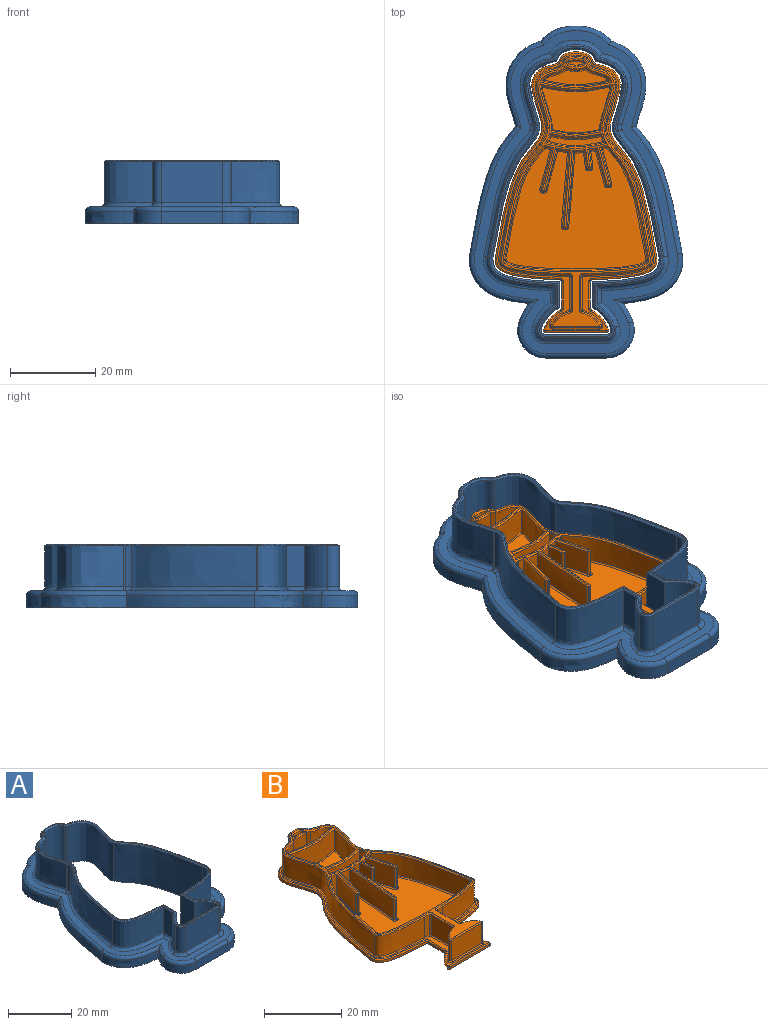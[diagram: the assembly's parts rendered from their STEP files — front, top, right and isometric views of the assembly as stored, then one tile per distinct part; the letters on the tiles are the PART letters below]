
ASSEMBLY  parts=2 mates=1
PART A: 111 faces, bbox 51.5x85.8x16.5 mm
  f0: extruded ~29.42x10.79mm, area 308.9mm2, adj f1,f13,f51,f75
  f1: extruded ~15.68x9.7mm, area 186.8mm2, adj f0,f29,f49,f73
  f2: cylinder r=9.66mm len=9.7mm, axis (0,0,-1), area 67.2mm2, adj f3,f29,f52,f69
  f3: cylinder r=2.09mm len=9.7mm, axis (0,0,-1), area 38.3mm2, adj f2,f4,f54,f67
  f4: plane 14.39x9.7mm, normal (0,-1,0), area 139.6mm2, adj f3,f5,f56,f68
  f5: cylinder r=2.09mm len=9.7mm, axis (0,0,-1), area 38.3mm2, adj f4,f6,f58,f70
  f6: cylinder r=9.66mm len=9.7mm, axis (0,0,-1), area 67.2mm2, adj f5,f30,f60,f72
  f7: extruded ~15.65x9.7mm, area 184.8mm2, adj f8,f30,f64,f76
  f8: plane 9.7x0.14mm, normal (-0.99,0.15,0), area 1.4mm2, adj f7,f31,f64,f66,f78
  f9: extruded ~9.7x0.34mm, area 3.3mm2, adj f10,f32,f61,f84
  f10: extruded ~15.59x9.7mm, area 189.2mm2, adj f9,f11,f59,f83
  f11: extruded ~10.77x9.7mm, area 126.7mm2, adj f10,f12,f57,f81
  f12: extruded ~15.59x9.7mm, area 189.2mm2, adj f11,f13,f55,f79
  f13: extruded ~9.7x1.79mm, area 17.6mm2, adj f0,f12,f53,f77
  f14: plane 14.65x6.04mm, normal (-1,0,0), area 88.5mm2, adj f15,f33,f35,f108
  f15: extruded ~15.68x14.65mm, area 270.2mm2, adj f14,f16,f35,f106
  f16: extruded ~29.26x14.65mm, area 464.1mm2, adj f15,f17,f35,f104
  f17: extruded ~16.71x14.65mm, area 298.4mm2, adj f16,f18,f35,f102
  f18: extruded ~14.71x0.53mm, area 10.7mm2, adj f17,f19,f35,f97,f102
  f19: extruded ~14.65x8.84mm, area 158.4mm2, adj f18,f20,f35,f97
  f20: extruded ~14.71x0.53mm, area 10.7mm2, adj f19,f21,f35,f97,f98
  f21: extruded ~16.71x14.65mm, area 298.4mm2, adj f20,f22,f35,f98
  f22: extruded ~29.33x14.65mm, area 465.2mm2, adj f21,f23,f35,f99
  f23: extruded ~15.66x14.65mm, area 268.6mm2, adj f22,f24,f35,f100
  f24: plane 14.65x6.04mm, normal (1,0,0), area 88.5mm2, adj f23,f25,f35,f101
  f25: cylinder r=8.56mm len=14.65mm, axis (0,0,-1), area 98.8mm2, adj f24,f26,f35,f103
  f26: cylinder r=0.99mm len=14.65mm, axis (0,0,-1), area 27.4mm2, adj f25,f27,f35,f105
  f27: plane 14.65x14.39mm, normal (0,1,0), area 210.8mm2, adj f26,f28,f35,f107
  f28: cylinder r=0.99mm len=14.65mm, axis (0,0,-1), area 27.4mm2, adj f27,f33,f35,f109
  f29: plane 9.7x4.33mm, normal (1,0,0), area 42mm2, adj f1,f2,f50,f71
  f30: plane 9.7x4.33mm, normal (-1,0,0), area 42mm2, adj f6,f7,f62,f74
  f31: extruded ~29.44x10.8mm, area 309.1mm2, adj f8,f32,f65,f80
  f32: extruded ~9.7x1.46mm, area 14.3mm2, adj f9,f31,f63,f82
  f33: cylinder r=8.56mm len=14.65mm, axis (0,0,-1), area 98.8mm2, adj f14,f28,f35,f110
  f34: plane 68.72x41.18mm, normal (0,0,1), area 81.6mm2, adj f49,f50,f51,f52,f53,f54,f55,f56
  f35: plane 77.87x50.07mm, normal (0,0,-1), area 1158.8mm2, adj f14,f15,f16,f17,f18,f19,f20,f21
  f36: extruded ~19.98x8.16mm, area 72.4mm2, adj f35,f37,f47,f95
  f37: extruded ~16.48x3.54mm, area 55.8mm2, adj f35,f36,f38,f93
  f38: extruded ~19.98x8.16mm, area 72.4mm2, adj f35,f37,f39,f91
  f39: extruded ~29.84x10.78mm, area 96.8mm2, adj f35,f38,f40,f89
  f40: extruded ~13.94x11.74mm, area 62.3mm2, adj f35,f39,f41,f87
  f41: cylinder r=14.06mm len=4.26mm, axis (0,0,-1), area 14.5mm2, adj f35,f40,f42,f85
  f42: cylinder r=6.49mm len=8.51mm, axis (0,0,-1), area 36.7mm2, adj f35,f41,f43,f86
  f43: plane 14.39x3mm, normal (0,-1,0), area 43.2mm2, adj f35,f42,f44,f88
  f44: cylinder r=6.49mm len=8.51mm, axis (0,0,-1), area 36.7mm2, adj f35,f43,f45,f90
  f45: cylinder r=14.06mm len=4.26mm, axis (0,0,-1), area 14.6mm2, adj f35,f44,f46,f92
  f46: extruded ~13.93x11.59mm, area 61.7mm2, adj f35,f45,f47,f94
  f47: extruded ~29.99x10.81mm, area 97.2mm2, adj f35,f36,f46,f96
  f48: plane 77.12x49.55mm, normal (0,0,1), area 462.9mm2, adj f67,f68,f69,f70,f71,f72,f73,f74
  f49: bspline ~17x7.57mm, area 8.6mm2, adj f1,f34,f50,f51
  f50: plane 4.83x0.33mm, normal (0.67,0,0.74), area 2mm2, adj f29,f34,f49,f52
  f51: bspline ~31.04x11.35mm, area 14.2mm2, adj f0,f34,f49,f53
  f52: cone r=9.66mm half-angle=47.7deg, axis (0,0,-1), area 3.1mm2, adj f2,f34,f50,f54
  f53: bspline ~1.96x0.54mm, area 0.8mm2, adj f13,f34,f51,f55
  f54: cone r=2.09mm half-angle=47.7deg, axis (0,0,-1), area 1.6mm2, adj f3,f34,f52,f56
  f55: bspline ~15.91x7.86mm, area 8.6mm2, adj f12,f34,f53,f57
  f56: plane 14.39x0.33mm, normal (0,-0.67,0.74), area 6.4mm2, adj f4,f34,f54,f58
  f57: bspline ~10.89x3.19mm, area 5.7mm2, adj f11,f34,f55,f59
  f58: cone r=2.09mm half-angle=47.7deg, axis (0,0,-1), area 1.6mm2, adj f5,f34,f56,f60
  f59: bspline ~15.91x7.86mm, area 8.6mm2, adj f10,f34,f57,f61
  f60: cone r=9.66mm half-angle=47.7deg, axis (0,0,-1), area 3.1mm2, adj f6,f34,f58,f62
  f61: bspline ~0.4x0.38mm, area 0.2mm2, adj f9,f34,f59,f63
  f62: plane 4.84x0.33mm, normal (-0.67,0,0.74), area 2mm2, adj f30,f34,f60,f64
  f63: bspline ~1.61x0.5mm, area 0.7mm2, adj f32,f34,f61,f65
  f64: bspline ~17.44x7.46mm, area 8.5mm2, adj f7,f8,f34,f62,f66
  f65: bspline ~32.87x11.64mm, area 14.2mm2, adj f31,f34,f63,f66
  f66: plane 0.34x0.3mm, normal (-0.66,0.1,0.74), area 0mm2, adj f8,f34,f64,f65
  f67: bspline ~17.16x8.58mm, area 7.8mm2, adj f3,f48,f68,f69
  f68: extruded ~14.39x1.1mm, area 23.7mm2, adj f4,f48,f67,f70
  f69: bspline ~23.72x23.72mm, area 11.3mm2, adj f2,f48,f67,f71
  f70: bspline ~4.18x3.19mm, area 7.8mm2, adj f5,f48,f68,f72
  f71: extruded ~4.33x1.1mm, area 5.9mm2, adj f29,f48,f69,f73
  f72: bspline ~23.72x23.72mm, area 11.3mm2, adj f6,f48,f70,f74
  f73: bspline ~16.94x8.46mm, area 32.1mm2, adj f1,f48,f71,f75
  f74: extruded ~4.33x1.1mm, area 5.9mm2, adj f30,f48,f72,f76
  f75: bspline ~29.96x11.92mm, area 52.6mm2, adj f0,f48,f73,f77
  f76: bspline ~16.92x8.24mm, area 31.7mm2, adj f7,f48,f74,f78
  f77: bspline ~1.79x1.19mm, area 2.6mm2, adj f13,f48,f75,f79
  f78: extruded ~1.11x1mm, area 0.2mm2, adj f8,f48,f76,f80
  f79: bspline ~16.88x7.89mm, area 32.8mm2, adj f12,f48,f77,f81
  f80: bspline ~29.99x11.93mm, area 52.7mm2, adj f31,f48,f78,f82
  f81: bspline ~12.89x4.11mm, area 22.3mm2, adj f11,f48,f79,f83
  f82: bspline ~1.46x1.18mm, area 2.1mm2, adj f32,f48,f80,f84
  f83: bspline ~16.88x7.89mm, area 32.8mm2, adj f10,f48,f81,f84
  f84: bspline ~1.14x1mm, area 0.5mm2, adj f9,f48,f82,f83
  f85: bspline ~28.12x28.12mm, area 9.8mm2, adj f41,f48,f86,f87
  f86: bspline ~25.96x12.98mm, area 18.9mm2, adj f42,f48,f85,f88
  f87: bspline ~16.36x12.12mm, area 35mm2, adj f40,f48,f85,f89
  f88: extruded ~14.39x1.1mm, area 23.7mm2, adj f43,f48,f86,f90
  f89: bspline ~30.77x12.11mm, area 53.3mm2, adj f39,f48,f87,f91
  f90: bspline ~8.51x6.49mm, area 18.9mm2, adj f44,f48,f88,f92
  f91: bspline ~20.56x8.81mm, area 39.5mm2, adj f38,f48,f89,f93
  f92: bspline ~28.12x28.12mm, area 9.8mm2, adj f45,f48,f90,f94
  f93: bspline ~17.04x4.59mm, area 30mm2, adj f37,f48,f91,f95
  f94: bspline ~16.34x11.96mm, area 34.7mm2, adj f46,f48,f92,f96
  f95: bspline ~20.56x8.81mm, area 39.5mm2, adj f36,f48,f93,f96
  f96: bspline ~30.72x12.1mm, area 53.6mm2, adj f47,f48,f94,f95
  f97: bspline ~9.95x3.4mm, area 6.1mm2, adj f18,f19,f20,f34,f98,f102
  f98: bspline ~17.35x7.19mm, area 10.9mm2, adj f20,f21,f34,f97,f99
  f99: bspline ~29.45x11.15mm, area 16.5mm2, adj f22,f34,f98,f100
  f100: bspline ~17.11x6.15mm, area 9.6mm2, adj f23,f34,f99,f101
  f101: plane 6.04x0.39mm, normal (0.67,0,0.74), area 3mm2, adj f24,f34,f100,f103
  f102: bspline ~17.35x7.19mm, area 10.9mm2, adj f17,f18,f34,f97,f104
  f103: cone r=8.94mm half-angle=47.7deg, axis (0,0,1), area 3.5mm2, adj f25,f34,f101,f105
  f104: bspline ~30.95x11.38mm, area 16.5mm2, adj f16,f34,f102,f106
  f105: cone r=1.38mm half-angle=47.7deg, axis (0,0,1), area 1.2mm2, adj f26,f34,f103,f107
  f106: bspline ~17.04x6.75mm, area 9.7mm2, adj f15,f34,f104,f108
  f107: plane 14.39x0.39mm, normal (0,0.67,0.74), area 7.5mm2, adj f27,f34,f105,f109
  f108: plane 6.04x0.39mm, normal (-0.67,0,0.74), area 3mm2, adj f14,f34,f106,f110
  f109: cone r=1.38mm half-angle=47.7deg, axis (0,0,1), area 1.2mm2, adj f28,f34,f107,f110
  f110: cone r=8.94mm half-angle=47.7deg, axis (0,0,1), area 3.5mm2, adj f33,f34,f108,f109
PART B: 264 faces, bbox 38.5x68.2x8.5 mm
  f0: plane 6.21x0.7mm, normal (1,0,0), area 4.3mm2, adj f1,f261,f262,f263
  f1: plane 65.77x37.97mm, normal (0,0,-1), area 1480.6mm2, adj f0,f2,f249,f250,f251,f252,f253,f254
  f2: cylinder r=0.44mm len=0.7mm, axis (0,0,-1), area 0.6mm2, adj f1,f3,f249,f260
  f3: bspline ~0.58x0.44mm, area 0.3mm2, adj f2,f4,f16,f248
  f4: extruded ~14.39x0.33mm, area 7.1mm2, adj f3,f5,f16,f260
  f5: bspline ~1.76x0.88mm, area 0.3mm2, adj f4,f6,f16,f259
  f6: bspline ~16.02x16.02mm, area 3.1mm2, adj f5,f7,f16,f258
  f7: bspline ~2.2x2.2mm, area 0.3mm2, adj f6,f8,f16,f257
  f8: extruded ~6.21x0.33mm, area 3.1mm2, adj f7,f9,f16,f256
  f9: bspline ~2.2x2.2mm, area 0.4mm2, adj f8,f10,f16,f255
  f10: bspline ~15.29x5.04mm, area 8.6mm2, adj f9,f11,f16,f254
  f11: bspline ~47.06x15.53mm, area 26.3mm2, adj f10,f12,f16,f253
  f12: bspline ~7.84x2.2mm, area 4.5mm2, adj f11,f13,f16,f252
  f13: bspline ~47x15.52mm, area 26.2mm2, adj f12,f14,f16,f251
  f14: bspline ~15.27x5.21mm, area 8.6mm2, adj f13,f15,f16,f250
  f15: bspline ~4.4x2.2mm, area 0.4mm2, adj f14,f16,f262,f263
  f16: plane 65.52x37.83mm, normal (0,0,1), area 91.8mm2, adj f3,f4,f5,f6,f7,f8,f9,f10
  f17: bspline ~4.4x2.2mm, area 0.3mm2, adj f16,f248,f261,f262
  f18: extruded ~10.94x0.33mm, area 5.4mm2, adj f16,f19,f227,f247
  f19: plane 10.94x6.4mm, normal (0,-1,0), area 70mm2, adj f18,f20,f225,f226
  f20: plane 10.94x0.33mm, normal (0,-0.67,0.74), area 4.9mm2, adj f19,f21,f60,f224
  f21: cone r=0.44mm half-angle=47.7deg, axis (0,0,-1), area 0.3mm2, adj f20,f22,f60,f226
  f22: cone r=6.91mm half-angle=47.7deg, axis (0,0,-1), area 2.4mm2, adj f21,f23,f59,f60
  f23: cylinder r=6.91mm len=6.4mm, axis (0,0,-1), area 35.2mm2, adj f22,f24,f226,f246
  f24: cylinder r=0.44mm len=6.4mm, axis (0,0,-1), area 3.8mm2, adj f23,f25,f59,f245
  f25: plane 7.66x6.4mm, normal (-1,0,0), area 49mm2, adj f24,f26,f58,f244
  f26: plane 7.66x0.33mm, normal (-0.67,0,0.74), area 3.4mm2, adj f25,f27,f59,f60
  f27: cone r=0.77mm half-angle=47.7deg, axis (0,0,1), area 0.4mm2, adj f26,f28,f58,f60
  f28: bspline ~1.77x0.36mm, area 0.8mm2, adj f27,f29,f57,f60
  f29: extruded ~6.4x1.77mm, area 11.3mm2, adj f28,f30,f58,f242
  f30: extruded ~14.57x6.4mm, area 102.6mm2, adj f29,f31,f57,f241
  f31: extruded ~41.68x10.97mm, area 284.7mm2, adj f30,f32,f56,f240
  f32: extruded ~6.4x5.32mm, area 42.2mm2, adj f31,f33,f55,f239
  f33: extruded ~6.4x1.2mm, area 10mm2, adj f32,f34,f54,f238
  f34: extruded ~6.4x5.72mm, area 43.1mm2, adj f33,f35,f53,f237
  f35: extruded ~6.4x1.2mm, area 10mm2, adj f34,f36,f52,f236
  f36: bspline ~1.5x1.27mm, area 0.8mm2, adj f35,f37,f53,f60
  f37: bspline ~5.49x3.41mm, area 2.9mm2, adj f36,f38,f52,f60
  f38: bspline ~43.88x11.71mm, area 19.8mm2, adj f37,f39,f51,f60
  f39: extruded ~41.64x10.96mm, area 284.5mm2, adj f38,f40,f52,f234
  f40: extruded ~14.59x6.4mm, area 103mm2, adj f39,f41,f51,f233
  f41: extruded ~6.4x1.77mm, area 11.3mm2, adj f40,f42,f50,f232
  f42: cylinder r=0.44mm len=6.4mm, axis (0,0,-1), area 4.4mm2, adj f41,f43,f49,f231
  f43: plane 7.66x6.4mm, normal (1,0,0), area 49mm2, adj f42,f44,f48,f230
  f44: plane 7.66x0.33mm, normal (0.67,0,0.74), area 3.4mm2, adj f43,f45,f49,f60
  f45: cone r=0.77mm half-angle=47.7deg, axis (0,0,1), area 0.4mm2, adj f44,f46,f48,f60
  f46: cone r=6.91mm half-angle=47.7deg, axis (0,0,-1), area 2.4mm2, adj f45,f47,f60,f224
  f47: cylinder r=6.91mm len=6.4mm, axis (0,0,-1), area 35.2mm2, adj f46,f48,f225,f228
  f48: cylinder r=0.44mm len=6.4mm, axis (0,0,-1), area 3.8mm2, adj f43,f45,f47,f229
  f49: cone r=0.77mm half-angle=47.7deg, axis (0,0,1), area 0.4mm2, adj f42,f44,f50,f60
  f50: bspline ~1.77x0.36mm, area 0.8mm2, adj f41,f49,f51,f60
  f51: bspline ~14.6x3.92mm, area 7.1mm2, adj f38,f40,f50,f60
  f52: extruded ~6.4x5.32mm, area 42.2mm2, adj f35,f37,f39,f235
  f53: bspline ~5.85x1.69mm, area 2.8mm2, adj f34,f36,f54,f60
  f54: bspline ~1.51x1.28mm, area 0.7mm2, adj f33,f53,f55,f60
  f55: bspline ~5.49x3.41mm, area 2.9mm2, adj f32,f54,f56,f60
  f56: bspline ~41.73x11.3mm, area 19.8mm2, adj f31,f55,f57,f60
  f57: bspline ~14.64x3.78mm, area 7mm2, adj f28,f30,f56,f60
  f58: cylinder r=0.44mm len=6.4mm, axis (0,0,-1), area 4.4mm2, adj f25,f27,f29,f243
  f59: cone r=0.77mm half-angle=47.7deg, axis (0,0,1), area 0.4mm2, adj f22,f24,f26,f60
  f60: plane 63.39x35.76mm, normal (0,0,1), area 151.5mm2, adj f20,f21,f22,f26,f27,f28,f36,f37
  f61: bspline ~4.24x1.65mm, area 3.9mm2, adj f60,f62
  f62: extruded ~6.7x3.6mm, area 52.3mm2, adj f61,f63
  f63: plane 3.6x1.66mm, normal (0,0,1), area 2.8mm2, adj f62
  f64: bspline ~5.66x1.18mm, area 2.2mm2, adj f60,f65,f78,f82
  f65: extruded ~6.4x4.72mm, area 31.5mm2, adj f64,f66,f76,f77
  f66: extruded ~6.4x0.82mm, area 7.1mm2, adj f65,f67,f75,f78
  f67: bspline ~1.09x1.04mm, area 0.5mm2, adj f66,f68,f74,f76
  f68: bspline ~4.99x2.58mm, area 2.6mm2, adj f67,f69,f74,f75
  f69: bspline ~16.15x1.45mm, area 7.7mm2, adj f68,f70,f73,f74
  f70: bspline ~4.99x2.58mm, area 2.6mm2, adj f69,f71,f72,f74
  f71: bspline ~1.09x1.04mm, area 0.5mm2, adj f70,f74,f76,f77
  f72: extruded ~6.4x4.8mm, area 35.4mm2, adj f70,f73,f77,f81
  f73: extruded ~15.96x6.4mm, area 103.4mm2, adj f69,f72,f75,f80
  f74: plane 15.2x3.78mm, normal (0,0,1), area 32.5mm2, adj f67,f68,f69,f70,f71,f76
  f75: extruded ~6.4x4.8mm, area 35.4mm2, adj f66,f68,f73,f79
  f76: bspline ~5.18x0.91mm, area 2.4mm2, adj f65,f67,f71,f74
  f77: extruded ~6.4x0.82mm, area 7.1mm2, adj f65,f71,f72,f82
  f78: bspline ~1.27x1.24mm, area 0.5mm2, adj f60,f64,f66,f79
  f79: bspline ~5.26x3.07mm, area 2.6mm2, adj f60,f75,f78,f80
  f80: bspline ~18.55x1.73mm, area 7.4mm2, adj f60,f73,f79,f81
  f81: bspline ~5.26x3.07mm, area 2.6mm2, adj f60,f72,f80,f82
  f82: bspline ~1.27x1.24mm, area 0.5mm2, adj f60,f64,f77,f81
  f83: bspline ~18.82x1.73mm, area 7.5mm2, adj f60,f84,f97,f101
  f84: extruded ~16.31x6.5mm, area 107.2mm2, adj f83,f85,f95,f96
  f85: extruded ~10.23x6.5mm, area 68.6mm2, adj f84,f86,f94,f97
  f86: bspline ~10.32x2.63mm, area 3.4mm2, adj f85,f87,f93,f95
  f87: bspline ~0.02x0.02mm, area 0mm2, adj f86,f88,f94
  f88: bspline ~11.25x0.98mm, area 3.7mm2, adj f87,f89,f91,f93
  f89: extruded ~11.25x6.5mm, area 73.9mm2, adj f88,f90,f94,f99
  f90: cylinder r=0.22mm len=6.5mm, axis (0,0,-1), area 2mm2, adj f89,f91,f96,f99,f101
  f91: bspline ~0.44x0.4mm, area 0mm2, adj f88,f90,f92
  f92: bspline ~10.32x2.63mm, area 3.4mm2, adj f91,f93,f95,f96
  f93: plane 16.1x10.99mm, normal (0,0,1), area 126.2mm2, adj f86,f88,f92,f95
  f94: cylinder r=0.22mm len=6.51mm, axis (0,0,-1), area 2mm2, adj f85,f87,f89,f97,f98
  f95: bspline ~16.6x1.36mm, area 5.4mm2, adj f84,f86,f92,f93
  f96: extruded ~10.23x6.5mm, area 68.6mm2, adj f84,f90,f92,f101
  f97: bspline ~12.31x2.79mm, area 4.9mm2, adj f60,f83,f85,f94,f98
  f98: plane 0.56x0.4mm, normal (0.12,0.66,0.74), area 0.1mm2, adj f60,f94,f97,f99
  f99: bspline ~12.38x1.32mm, area 5.2mm2, adj f60,f89,f90,f98,f100,f101
  f100: plane 0.39x0.33mm, normal (-0.13,0.66,0.74), area 0.1mm2, adj f60,f99,f101
  f101: bspline ~12.3x2.79mm, area 4.9mm2, adj f60,f83,f90,f96,f99,f100
  f102: bspline ~2.82x1.46mm, area 1mm2, adj f60,f103,f124,f132
  f103: extruded ~6.4x1.8mm, area 12.5mm2, adj f102,f104,f122,f123
  f104: extruded ~12.01x6.4mm, area 77.7mm2, adj f103,f105,f121,f132
  f105: bspline ~12.3x1.17mm, area 5.9mm2, adj f104,f106,f120,f122
  f106: bspline ~1.95x1.08mm, area 0.8mm2, adj f105,f107,f120,f121
  f107: bspline ~2.3x0.83mm, area 1mm2, adj f106,f108,f119,f120
  f108: bspline ~1.77x0.64mm, area 0.9mm2, adj f107,f109,f118,f120
  f109: bspline ~1.14x0.47mm, area 0.5mm2, adj f108,f110,f117,f120
  f110: bspline ~2.25x0.44mm, area 1.1mm2, adj f109,f111,f116,f120
  f111: bspline ~3.78x0.79mm, area 1.9mm2, adj f110,f112,f115,f120
  f112: bspline ~1.14x0.55mm, area 0.5mm2, adj f111,f113,f114,f120
  f113: bspline ~1.46x0.64mm, area 0.6mm2, adj f112,f120,f122,f123
  f114: extruded ~6.4x1.08mm, area 7mm2, adj f112,f115,f123,f125
  f115: extruded ~6.4x3.77mm, area 24.4mm2, adj f111,f114,f116,f126
  f116: extruded ~6.4x2.25mm, area 14.4mm2, adj f110,f115,f117,f127
  f117: extruded ~6.4x1.1mm, area 7.1mm2, adj f109,f116,f118,f128
  f118: extruded ~6.4x1.72mm, area 11.2mm2, adj f108,f117,f119,f129
  f119: extruded ~6.4x2.22mm, area 14.5mm2, adj f107,f118,f121,f130
  f120: plane 13.06x2.65mm, normal (0,0,1), area 15.9mm2, adj f105,f106,f107,f108,f109,f110,f111,f112
  f121: extruded ~6.4x1.76mm, area 12.3mm2, adj f104,f106,f119,f131
  f122: bspline ~1.99x1.1mm, area 0.8mm2, adj f103,f105,f113,f120
  f123: extruded ~6.4x1.38mm, area 9.1mm2, adj f103,f113,f114,f124
  f124: bspline ~1.98x0.77mm, area 0.7mm2, adj f60,f102,f123,f125
  f125: bspline ~1.15x0.55mm, area 0.5mm2, adj f60,f114,f124,f126
  f126: bspline ~3.84x0.8mm, area 1.7mm2, adj f60,f115,f125,f127
  f127: bspline ~2.3x0.44mm, area 1mm2, adj f60,f116,f126,f128
  f128: bspline ~1.15x0.47mm, area 0.5mm2, adj f60,f117,f127,f129
  f129: bspline ~1.79x0.64mm, area 0.8mm2, adj f60,f118,f128,f130
  f130: bspline ~2.85x0.96mm, area 1.1mm2, adj f60,f119,f129,f131
  f131: bspline ~2.77x1.43mm, area 1mm2, adj f60,f121,f130,f132
  f132: bspline ~13.86x1.36mm, area 5.5mm2, adj f60,f102,f104,f131
  f133: bspline ~17.93x1.79mm, area 8mm2, adj f60,f134,f195,f223
  f134: extruded ~17.59x6.4mm, area 113mm2, adj f133,f135,f193,f194
  f135: extruded ~6.4x2.56mm, area 16.4mm2, adj f134,f136,f192,f223
  f136: bspline ~2.64x0.47mm, area 1.1mm2, adj f135,f137,f191,f193
  f137: plane 33.35x28.72mm, normal (0,0,1), area 671.4mm2, adj f136,f138,f165,f166,f167,f168,f169,f170
  f138: extruded ~0.35x0.3mm, area 0.1mm2, adj f137,f139,f165,f190
  f139: plane 6.4x0.22mm, normal (-0.11,-0.99,0), area 1.4mm2, adj f138,f140,f194,f196
  f140: cylinder r=0.44mm len=6.4mm, axis (0,0,-1), area 4.4mm2, adj f139,f141,f190,f197
  f141: extruded ~17.54x6.4mm, area 112.6mm2, adj f140,f142,f189,f198
  f142: extruded ~6.4x2.87mm, area 18.6mm2, adj f141,f143,f188,f199
  f143: extruded ~9.59x6.4mm, area 63.6mm2, adj f142,f144,f187,f200
  f144: cylinder r=0.44mm len=6.4mm, axis (0,0,-1), area 4.4mm2, adj f143,f145,f186,f201
  f145: plane 6.4x0.21mm, normal (-0.33,-0.94,0), area 1.4mm2, adj f144,f146,f185,f202
  f146: cylinder r=0.44mm len=6.4mm, axis (0,0,-1), area 4.4mm2, adj f145,f147,f184,f203
  f147: extruded ~9.47x6.4mm, area 62.7mm2, adj f146,f148,f183,f204
  f148: extruded ~6.4x1.4mm, area 9.2mm2, adj f147,f149,f182,f205
  f149: plane 6.4x0.38mm, normal (-0.23,-0.97,0), area 2.5mm2, adj f148,f150,f181,f206
  f150: extruded ~26.48x9.36mm, area 182.8mm2, adj f149,f151,f180,f207
  f151: extruded ~33.54x6.4mm, area 223.3mm2, adj f150,f152,f179,f208
  f152: extruded ~26.53x9.4mm, area 183.2mm2, adj f151,f153,f178,f209
  f153: plane 6.4x0.37mm, normal (0.27,-0.96,0), area 2.5mm2, adj f152,f154,f177,f210
  f154: extruded ~6.4x1.16mm, area 7.6mm2, adj f153,f155,f176,f211
  f155: extruded ~8.32x6.4mm, area 55.1mm2, adj f154,f156,f175,f212
  f156: cylinder r=0.44mm len=6.4mm, axis (0,0,-1), area 4.4mm2, adj f155,f157,f174,f213
  f157: plane 6.4x0.21mm, normal (0.24,-0.97,0), area 1.4mm2, adj f156,f158,f173,f214
  f158: cylinder r=0.44mm len=6.4mm, axis (0,0,-1), area 4.4mm2, adj f157,f159,f172,f215
  f159: extruded ~8.36x6.4mm, area 55.4mm2, adj f158,f160,f171,f216
  f160: extruded ~6.4x1.7mm, area 11.1mm2, adj f159,f161,f170,f217
  f161: extruded ~6.4x3.88mm, area 25.1mm2, adj f160,f162,f169,f218
  f162: cylinder r=0.44mm len=6.4mm, axis (0,0,-1), area 4.4mm2, adj f161,f163,f168,f219
  f163: plane 6.4x0.22mm, normal (0.11,-0.99,0), area 1.4mm2, adj f162,f164,f167,f220
  f164: cylinder r=0.44mm len=6.4mm, axis (0,0,-1), area 4.4mm2, adj f163,f166,f192,f221
  f165: bspline ~2.2x2.2mm, area 0.4mm2, adj f137,f138,f193,f194
  f166: bspline ~2.2x2.2mm, area 0.4mm2, adj f137,f164,f167,f191
  f167: extruded ~0.35x0.3mm, area 0.1mm2, adj f137,f163,f166,f168
  f168: bspline ~0.88x0.72mm, area 0.4mm2, adj f137,f162,f167,f169
  f169: bspline ~3.97x0.89mm, area 1.9mm2, adj f137,f161,f168,f170
  f170: bspline ~1.79x0.65mm, area 0.7mm2, adj f137,f160,f169,f171
  f171: bspline ~8.49x2.55mm, area 4.2mm2, adj f137,f159,f170,f172
  f172: bspline ~2.2x2.2mm, area 0.4mm2, adj f137,f158,f171,f173
  f173: extruded ~0.37x0.3mm, area 0.1mm2, adj f137,f157,f172,f174
  f174: bspline ~0.94x0.67mm, area 0.4mm2, adj f137,f156,f173,f175
  f175: bspline ~8.45x2.54mm, area 4.2mm2, adj f137,f155,f174,f176
  f176: bspline ~1.26x0.6mm, area 0.5mm2, adj f137,f154,f175,f177
  f177: extruded ~0.47x0.42mm, area 0.1mm2, adj f137,f153,f176,f178
  f178: bspline ~26.91x9.8mm, area 14.1mm2, adj f137,f152,f177,f179
  f179: bspline ~33.57x2.58mm, area 17.1mm2, adj f137,f151,f178,f180
  f180: bspline ~26.85x9.76mm, area 14.1mm2, adj f137,f150,f179,f181
  f181: extruded ~0.46x0.41mm, area 0.1mm2, adj f137,f149,f180,f182
  f182: bspline ~1.49x0.65mm, area 0.6mm2, adj f137,f148,f181,f183
  f183: bspline ~9.6x2.85mm, area 4.8mm2, adj f137,f147,f182,f184
  f184: bspline ~4.4x2.2mm, area 0.4mm2, adj f137,f146,f183,f185
  f185: extruded ~0.38x0.32mm, area 0.1mm2, adj f137,f145,f184,f186
  f186: bspline ~2.2x2.2mm, area 0.4mm2, adj f137,f144,f185,f187
  f187: bspline ~9.76x2.89mm, area 4.8mm2, adj f137,f143,f186,f188
  f188: bspline ~2.97x0.77mm, area 1.3mm2, adj f137,f142,f187,f189
  f189: bspline ~17.66x1.77mm, area 8.6mm2, adj f137,f141,f188,f190
  f190: bspline ~4.4x2.2mm, area 0.4mm2, adj f137,f138,f140,f189
  f191: bspline ~3.9x0.88mm, area 1.9mm2, adj f136,f137,f166,f192
  f192: extruded ~6.4x3.85mm, area 24.9mm2, adj f135,f164,f191,f222
  f193: bspline ~17.73x1.78mm, area 8.7mm2, adj f134,f136,f137,f165
  f194: cylinder r=0.44mm len=6.4mm, axis (0,0,-1), area 4.4mm2, adj f134,f139,f165,f195
  f195: cone r=0.44mm half-angle=47.7deg, axis (0,0,-1), area 0.2mm2, adj f60,f133,f194,f196
  f196: plane 0.35x0.3mm, normal (-0.07,-0.67,0.74), area 0.1mm2, adj f60,f139,f195,f197
  f197: cone r=0.44mm half-angle=47.7deg, axis (0,0,-1), area 0.2mm2, adj f60,f140,f196,f198
  f198: bspline ~18.78x1.82mm, area 7.9mm2, adj f60,f141,f197,f199
  f199: bspline ~3.87x0.89mm, area 1.4mm2, adj f60,f142,f198,f200
  f200: bspline ~10.48x3.05mm, area 4.5mm2, adj f60,f143,f199,f201
  f201: cone r=0.44mm half-angle=47.7deg, axis (0,0,-1), area 0.2mm2, adj f60,f144,f200,f202
  f202: plane 0.38x0.32mm, normal (-0.22,-0.64,0.74), area 0.1mm2, adj f60,f145,f201,f203
  f203: cone r=0.44mm half-angle=47.7deg, axis (0,0,-1), area 0.2mm2, adj f60,f146,f202,f204
  f204: bspline ~10.39x3.02mm, area 4.4mm2, adj f60,f147,f203,f205
  f205: bspline ~1.9x0.74mm, area 0.7mm2, adj f60,f148,f204,f206
  f206: plane 0.6x0.46mm, normal (-0.15,-0.65,0.74), area 0.2mm2, adj f60,f149,f205,f207
  f207: bspline ~29.47x10.89mm, area 12.8mm2, adj f60,f150,f206,f208
  f208: bspline ~34.24x3.31mm, area 15.8mm2, adj f60,f151,f207,f209
  f209: bspline ~29.54x10.93mm, area 12.8mm2, adj f60,f152,f208,f210
  f210: plane 0.59x0.5mm, normal (0.18,-0.65,0.74), area 0.2mm2, adj f60,f153,f209,f211
  f211: bspline ~1.7x0.7mm, area 0.6mm2, adj f60,f154,f210,f212
  f212: bspline ~9.16x2.71mm, area 3.9mm2, adj f60,f155,f211,f213
  f213: cone r=0.44mm half-angle=47.7deg, axis (0,0,-1), area 0.2mm2, adj f60,f156,f212,f214
  f214: plane 0.37x0.3mm, normal (0.16,-0.65,0.74), area 0.1mm2, adj f60,f157,f213,f215
  f215: cone r=0.44mm half-angle=47.7deg, axis (0,0,-1), area 0.2mm2, adj f60,f158,f214,f216
  f216: bspline ~9.19x2.71mm, area 3.9mm2, adj f60,f159,f215,f217
  f217: bspline ~2.65x0.8mm, area 0.9mm2, adj f60,f160,f216,f218
  f218: bspline ~4.25x0.95mm, area 1.8mm2, adj f60,f161,f217,f219
  f219: cone r=0.44mm half-angle=47.7deg, axis (0,0,-1), area 0.2mm2, adj f60,f162,f218,f220
  f220: plane 0.35x0.3mm, normal (0.07,-0.67,0.74), area 0.1mm2, adj f60,f163,f219,f221
  f221: cone r=0.44mm half-angle=47.7deg, axis (0,0,-1), area 0.2mm2, adj f60,f164,f220,f222
  f222: bspline ~4.41x0.99mm, area 1.8mm2, adj f60,f192,f221,f223
  f223: bspline ~3.5x0.54mm, area 1.3mm2, adj f60,f133,f135,f222
  f224: cone r=0.44mm half-angle=47.7deg, axis (0,0,-1), area 0.3mm2, adj f20,f46,f60,f225
  f225: cylinder r=0.44mm len=6.4mm, axis (0,0,-1), area 6mm2, adj f19,f47,f224,f227
  f226: cylinder r=0.44mm len=6.4mm, axis (0,0,-1), area 6mm2, adj f19,f21,f23,f247
  f227: bspline ~1.18x0.77mm, area 0.6mm2, adj f16,f18,f225,f228
  f228: bspline ~15.14x15.14mm, area 2.8mm2, adj f16,f47,f227,f229
  f229: bspline ~1.76x0.88mm, area 0.2mm2, adj f16,f48,f228,f230
  f230: extruded ~7.66x0.33mm, area 3.8mm2, adj f16,f43,f229,f231
  f231: bspline ~0.88x0.88mm, area 0.2mm2, adj f16,f42,f230,f232
  f232: bspline ~1.77x0.36mm, area 0.9mm2, adj f16,f41,f231,f233
  f233: bspline ~14.93x4.32mm, area 8.1mm2, adj f16,f40,f232,f234
  f234: bspline ~41.99x11.34mm, area 22mm2, adj f16,f39,f233,f235
  f235: bspline ~5.64x3.61mm, area 3.3mm2, adj f16,f52,f234,f236
  f236: bspline ~1.33x1.13mm, area 0.7mm2, adj f16,f35,f235,f237
  f237: bspline ~6.39x1.67mm, area 3.5mm2, adj f16,f34,f236,f238
  f238: bspline ~1.33x1.13mm, area 0.7mm2, adj f16,f33,f237,f239
  f239: bspline ~5.64x3.61mm, area 3.3mm2, adj f16,f32,f238,f240
  f240: bspline ~41.76x11.31mm, area 22mm2, adj f16,f31,f239,f241
  f241: bspline ~14.92x4.27mm, area 8mm2, adj f16,f30,f240,f242
  f242: bspline ~1.77x0.36mm, area 0.9mm2, adj f16,f29,f241,f243
  f243: bspline ~0.88x0.88mm, area 0.2mm2, adj f16,f58,f242,f244
  f244: extruded ~7.66x0.33mm, area 3.8mm2, adj f16,f25,f243,f245
  f245: bspline ~0.88x0.88mm, area 0.2mm2, adj f16,f24,f244,f246
  f246: bspline ~15.14x15.14mm, area 2.8mm2, adj f16,f23,f245,f247
  f247: bspline ~4.4x2.2mm, area 0.6mm2, adj f16,f18,f226,f246
  f248: bspline ~16.02x16.02mm, area 3.1mm2, adj f3,f16,f17,f249
  f249: cylinder r=8.01mm len=4.69mm, axis (0,0,-1), area 4.5mm2, adj f1,f2,f248,f261
  f250: extruded ~15.25x5.1mm, area 12.3mm2, adj f1,f14,f251,f263
  f251: extruded ~46.32x15.03mm, area 36.6mm2, adj f1,f13,f250,f252
  f252: extruded ~7.8x2.03mm, area 6.6mm2, adj f1,f12,f251,f253
  f253: extruded ~46.38x15.04mm, area 36.6mm2, adj f1,f11,f252,f254
  f254: extruded ~15.23x5.04mm, area 12.3mm2, adj f1,f10,f253,f255
  f255: cylinder r=0.44mm len=0.7mm, axis (0,0,-1), area 0.5mm2, adj f1,f9,f254,f256
  f256: plane 6.21x0.7mm, normal (-1,0,0), area 4.3mm2, adj f1,f8,f255,f257
  f257: cylinder r=0.44mm len=0.7mm, axis (0,0,-1), area 0.3mm2, adj f1,f7,f256,f258
  f258: cylinder r=8.01mm len=4.69mm, axis (0,0,-1), area 4.5mm2, adj f1,f6,f257,f259
  f259: cylinder r=0.44mm len=0.7mm, axis (0,0,-1), area 0.6mm2, adj f1,f5,f258,f260
  f260: plane 14.39x0.7mm, normal (0,-1,0), area 10.1mm2, adj f1,f2,f4,f259
  f261: cylinder r=0.44mm len=0.7mm, axis (0,0,-1), area 0.3mm2, adj f0,f1,f17,f249
  f262: extruded ~6.21x0.33mm, area 3.1mm2, adj f0,f15,f16,f17
  f263: cylinder r=0.44mm len=0.7mm, axis (0,0,-1), area 0.5mm2, adj f0,f1,f15,f250
PLACE A t=(-11.45,19.34,-0.96)mm
PLACE B t=(-12,14.72,-0.96)mm
MATE fastened B.f1 <-> A.f35  axis (0,0,-1) through (-11.9,-1.62,-0.96)mm
